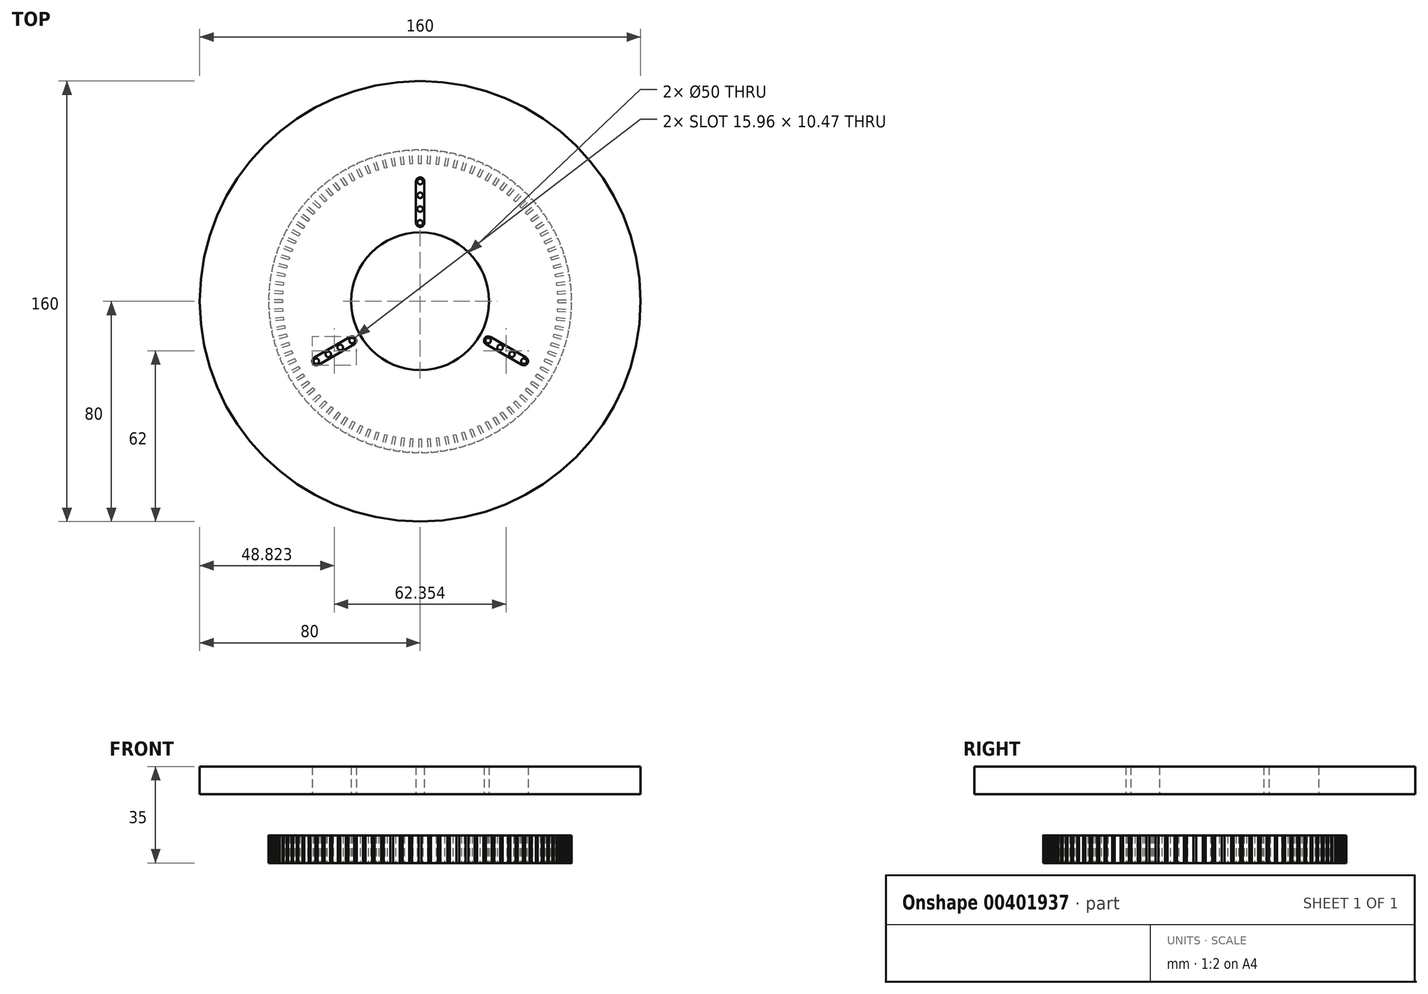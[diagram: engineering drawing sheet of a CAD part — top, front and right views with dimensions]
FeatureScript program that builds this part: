
annotation { "Feature Type Name" : "Feature", "Feature Type Description" : "" }
export const myFeature = defineFeature(function(context is Context, id is Id, definition is map)
    precondition{}
    {
        {
            var Q0;
            Q0=qCreatedBy(makeId("Top.planeOp"),FACE);
            var sketch = newSketch(context, id + "F0", { "sketchPlane" : qUnion([Q0])});
            skCircle(sketch, "E0", {"center": v(0, 0) * mm, "radius": 55 * mm});
            skCircle(sketch, "E1", {"center": v(0, 0) * mm, "radius": 25 * mm});
            skLineSegment(sketch, "E2.bottom", {"start": v(0.5, 50) * mm, "end": v(-0.5, 50) * mm});
            skLineSegment(sketch, "E2.top", {"start": v(0.5, 60) * mm, "end": v(-0.5, 60) * mm});
            skLineSegment(sketch, "E2.left", {"start": v(0.5, 50) * mm, "end": v(0.5, 60) * mm});
            skLineSegment(sketch, "E2.right", {"start": v(-0.5, 50) * mm, "end": v(-0.5, 60) * mm});
            skPoint(sketch, "E2.middle", {"position": v(0, 55) * mm});
            skLineSegment(sketch, "E3.1.0", {"start": v(-2.64, 49.93) * mm, "end": v(-3.27, 59.91) * mm});
            skLineSegment(sketch, "E3.1.1", {"start": v(-2.64, 49.93) * mm, "end": v(-3.64, 49.87) * mm});
            skLineSegment(sketch, "E3.1.2", {"start": v(-3.64, 49.87) * mm, "end": v(-4.27, 59.85) * mm});
            skLineSegment(sketch, "E3.1.3", {"start": v(-3.27, 59.91) * mm, "end": v(-4.27, 59.85) * mm});
            skLineSegment(sketch, "E3.2.0", {"start": v(-5.77, 49.67) * mm, "end": v(-7.02, 59.59) * mm});
            skLineSegment(sketch, "E3.2.1", {"start": v(-5.77, 49.67) * mm, "end": v(-6.76, 49.54) * mm});
            skLineSegment(sketch, "E3.2.2", {"start": v(-6.76, 49.54) * mm, "end": v(-8.02, 59.46) * mm});
            skLineSegment(sketch, "E3.2.3", {"start": v(-7.02, 59.59) * mm, "end": v(-8.02, 59.46) * mm});
            skLineSegment(sketch, "E4.1.3.0", {"start": v(-8.88, 49.2) * mm, "end": v(-10.75, 59.03) * mm});
            skLineSegment(sketch, "E4.3.3.0", {"start": v(-8.88, 49.2) * mm, "end": v(-9.86, 49.02) * mm});
            skLineSegment(sketch, "E4.6.3.0", {"start": v(-9.86, 49.02) * mm, "end": v(-11.73, 58.84) * mm});
            skLineSegment(sketch, "E4.9.3.0", {"start": v(-10.75, 59.03) * mm, "end": v(-11.73, 58.84) * mm});
            skLineSegment(sketch, "E4.1.4.0", {"start": v(-11.95, 48.55) * mm, "end": v(-14.44, 58.24) * mm});
            skLineSegment(sketch, "E4.3.4.0", {"start": v(-11.95, 48.55) * mm, "end": v(-12.92, 48.3) * mm});
            skLineSegment(sketch, "E4.6.4.0", {"start": v(-12.92, 48.3) * mm, "end": v(-15.4, 58) * mm});
            skLineSegment(sketch, "E4.9.4.0", {"start": v(-14.44, 58.24) * mm, "end": v(-15.4, 58) * mm});
            skLineSegment(sketch, "E4.1.5.0", {"start": v(-14.98, 47.7) * mm, "end": v(-18.07, 57.22) * mm});
            skLineSegment(sketch, "E4.3.5.0", {"start": v(-14.98, 47.7) * mm, "end": v(-15.93, 47.4) * mm});
            skLineSegment(sketch, "E4.6.5.0", {"start": v(-15.93, 47.4) * mm, "end": v(-19.02, 56.9) * mm});
            skLineSegment(sketch, "E4.9.5.0", {"start": v(-18.07, 57.22) * mm, "end": v(-19.02, 56.9) * mm});
            skLineSegment(sketch, "E4.1.6.0", {"start": v(-17.94, 46.67) * mm, "end": v(-21.62, 55.97) * mm});
            skLineSegment(sketch, "E4.3.6.0", {"start": v(-17.94, 46.67) * mm, "end": v(-18.87, 46.3) * mm});
            skLineSegment(sketch, "E4.6.6.0", {"start": v(-18.87, 46.3) * mm, "end": v(-22.55, 55.6) * mm});
            skLineSegment(sketch, "E4.9.6.0", {"start": v(-21.62, 55.97) * mm, "end": v(-22.55, 55.6) * mm});
            skLineSegment(sketch, "E4.1.7.0", {"start": v(-20.84, 45.45) * mm, "end": v(-25.1, 54.5) * mm});
            skLineSegment(sketch, "E4.3.7.0", {"start": v(-20.84, 45.45) * mm, "end": v(-21.74, 45.03) * mm});
            skLineSegment(sketch, "E4.6.7.0", {"start": v(-21.74, 45.03) * mm, "end": v(-26, 54.08) * mm});
            skLineSegment(sketch, "E4.9.7.0", {"start": v(-25.1, 54.5) * mm, "end": v(-26, 54.08) * mm});
            skLineSegment(sketch, "E4.1.8.0", {"start": v(-23.65, 44.06) * mm, "end": v(-28.47, 52.82) * mm});
            skLineSegment(sketch, "E4.3.8.0", {"start": v(-23.65, 44.06) * mm, "end": v(-24.53, 43.57) * mm});
            skLineSegment(sketch, "E4.6.8.0", {"start": v(-24.53, 43.57) * mm, "end": v(-29.34, 52.34) * mm});
            skLineSegment(sketch, "E4.9.8.0", {"start": v(-28.47, 52.82) * mm, "end": v(-29.34, 52.34) * mm});
            skLineSegment(sketch, "E4.1.9.0", {"start": v(-26.37, 42.48) * mm, "end": v(-31.73, 50.93) * mm});
            skLineSegment(sketch, "E4.3.9.0", {"start": v(-26.37, 42.48) * mm, "end": v(-27.21, 41.95) * mm});
            skLineSegment(sketch, "E4.6.9.0", {"start": v(-27.21, 41.95) * mm, "end": v(-32.57, 50.4) * mm});
            skLineSegment(sketch, "E4.9.9.0", {"start": v(-31.73, 50.93) * mm, "end": v(-32.57, 50.4) * mm});
            skLineSegment(sketch, "E4.1.10.0", {"start": v(-28.98, 40.74) * mm, "end": v(-34.86, 48.83) * mm});
            skLineSegment(sketch, "E4.3.10.0", {"start": v(-28.98, 40.74) * mm, "end": v(-29.8, 40.16) * mm});
            skLineSegment(sketch, "E4.6.10.0", {"start": v(-29.8, 40.16) * mm, "end": v(-35.67, 48.25) * mm});
            skLineSegment(sketch, "E4.9.10.0", {"start": v(-34.86, 48.83) * mm, "end": v(-35.67, 48.25) * mm});
            skLineSegment(sketch, "E4.1.11.0", {"start": v(-31.49, 38.84) * mm, "end": v(-37.86, 46.55) * mm});
            skLineSegment(sketch, "E4.3.11.0", {"start": v(-31.49, 38.84) * mm, "end": v(-32.26, 38.2) * mm});
            skLineSegment(sketch, "E4.6.11.0", {"start": v(-32.26, 38.2) * mm, "end": v(-38.63, 45.91) * mm});
            skLineSegment(sketch, "E4.9.11.0", {"start": v(-37.86, 46.55) * mm, "end": v(-38.63, 45.91) * mm});
            skLineSegment(sketch, "E4.1.12.0", {"start": v(-33.86, 36.8) * mm, "end": v(-40.7, 44.08) * mm});
            skLineSegment(sketch, "E4.3.12.0", {"start": v(-33.86, 36.8) * mm, "end": v(-34.6, 36.1) * mm});
            skLineSegment(sketch, "E4.6.12.0", {"start": v(-34.6, 36.1) * mm, "end": v(-41.44, 43.4) * mm});
            skLineSegment(sketch, "E4.9.12.0", {"start": v(-40.7, 44.08) * mm, "end": v(-41.44, 43.4) * mm});
            skLineSegment(sketch, "E4.1.13.0", {"start": v(-36.1, 34.6) * mm, "end": v(-43.4, 41.44) * mm});
            skLineSegment(sketch, "E4.3.13.0", {"start": v(-36.1, 34.6) * mm, "end": v(-36.8, 33.86) * mm});
            skLineSegment(sketch, "E4.6.13.0", {"start": v(-36.8, 33.86) * mm, "end": v(-44.08, 40.7) * mm});
            skLineSegment(sketch, "E4.9.13.0", {"start": v(-43.4, 41.44) * mm, "end": v(-44.08, 40.7) * mm});
            skLineSegment(sketch, "E4.1.14.0", {"start": v(-38.2, 32.26) * mm, "end": v(-45.91, 38.63) * mm});
            skLineSegment(sketch, "E4.3.14.0", {"start": v(-38.2, 32.26) * mm, "end": v(-38.84, 31.49) * mm});
            skLineSegment(sketch, "E4.6.14.0", {"start": v(-38.84, 31.49) * mm, "end": v(-46.55, 37.86) * mm});
            skLineSegment(sketch, "E4.9.14.0", {"start": v(-45.91, 38.63) * mm, "end": v(-46.55, 37.86) * mm});
            skLineSegment(sketch, "E4.1.15.0", {"start": v(-40.16, 29.8) * mm, "end": v(-48.25, 35.67) * mm});
            skLineSegment(sketch, "E4.3.15.0", {"start": v(-40.16, 29.8) * mm, "end": v(-40.74, 28.98) * mm});
            skLineSegment(sketch, "E4.6.15.0", {"start": v(-40.74, 28.98) * mm, "end": v(-48.83, 34.86) * mm});
            skLineSegment(sketch, "E4.9.15.0", {"start": v(-48.25, 35.67) * mm, "end": v(-48.83, 34.86) * mm});
            skLineSegment(sketch, "E4.1.16.0", {"start": v(-41.95, 27.21) * mm, "end": v(-50.4, 32.57) * mm});
            skLineSegment(sketch, "E4.3.16.0", {"start": v(-41.95, 27.21) * mm, "end": v(-42.48, 26.37) * mm});
            skLineSegment(sketch, "E4.6.16.0", {"start": v(-42.48, 26.37) * mm, "end": v(-50.93, 31.73) * mm});
            skLineSegment(sketch, "E4.9.16.0", {"start": v(-50.4, 32.57) * mm, "end": v(-50.93, 31.73) * mm});
            skLineSegment(sketch, "E4.1.17.0", {"start": v(-43.57, 24.53) * mm, "end": v(-52.34, 29.34) * mm});
            skLineSegment(sketch, "E4.3.17.0", {"start": v(-43.57, 24.53) * mm, "end": v(-44.06, 23.65) * mm});
            skLineSegment(sketch, "E4.6.17.0", {"start": v(-44.06, 23.65) * mm, "end": v(-52.82, 28.47) * mm});
            skLineSegment(sketch, "E4.9.17.0", {"start": v(-52.34, 29.34) * mm, "end": v(-52.82, 28.47) * mm});
            skLineSegment(sketch, "E4.1.18.0", {"start": v(-45.03, 21.74) * mm, "end": v(-54.08, 26) * mm});
            skLineSegment(sketch, "E4.3.18.0", {"start": v(-45.03, 21.74) * mm, "end": v(-45.45, 20.84) * mm});
            skLineSegment(sketch, "E4.6.18.0", {"start": v(-45.45, 20.84) * mm, "end": v(-54.5, 25.1) * mm});
            skLineSegment(sketch, "E4.9.18.0", {"start": v(-54.08, 26) * mm, "end": v(-54.5, 25.1) * mm});
            skLineSegment(sketch, "E4.1.19.0", {"start": v(-46.3, 18.87) * mm, "end": v(-55.6, 22.55) * mm});
            skLineSegment(sketch, "E4.3.19.0", {"start": v(-46.3, 18.87) * mm, "end": v(-46.67, 17.94) * mm});
            skLineSegment(sketch, "E4.6.19.0", {"start": v(-46.67, 17.94) * mm, "end": v(-55.97, 21.62) * mm});
            skLineSegment(sketch, "E4.9.19.0", {"start": v(-55.6, 22.55) * mm, "end": v(-55.97, 21.62) * mm});
            skLineSegment(sketch, "E4.1.20.0", {"start": v(-47.4, 15.93) * mm, "end": v(-56.9, 19.02) * mm});
            skLineSegment(sketch, "E4.3.20.0", {"start": v(-47.4, 15.93) * mm, "end": v(-47.7, 14.98) * mm});
            skLineSegment(sketch, "E4.6.20.0", {"start": v(-47.7, 14.98) * mm, "end": v(-57.22, 18.07) * mm});
            skLineSegment(sketch, "E4.9.20.0", {"start": v(-56.9, 19.02) * mm, "end": v(-57.22, 18.07) * mm});
            skLineSegment(sketch, "E4.1.21.0", {"start": v(-48.3, 12.92) * mm, "end": v(-58, 15.4) * mm});
            skLineSegment(sketch, "E4.3.21.0", {"start": v(-48.3, 12.92) * mm, "end": v(-48.55, 11.95) * mm});
            skLineSegment(sketch, "E4.6.21.0", {"start": v(-48.55, 11.95) * mm, "end": v(-58.24, 14.44) * mm});
            skLineSegment(sketch, "E4.9.21.0", {"start": v(-58, 15.4) * mm, "end": v(-58.24, 14.44) * mm});
            skLineSegment(sketch, "E4.1.22.0", {"start": v(-49.02, 9.86) * mm, "end": v(-58.84, 11.73) * mm});
            skLineSegment(sketch, "E4.3.22.0", {"start": v(-49.02, 9.86) * mm, "end": v(-49.2, 8.88) * mm});
            skLineSegment(sketch, "E4.6.22.0", {"start": v(-49.2, 8.88) * mm, "end": v(-59.03, 10.75) * mm});
            skLineSegment(sketch, "E4.9.22.0", {"start": v(-58.84, 11.73) * mm, "end": v(-59.03, 10.75) * mm});
            skLineSegment(sketch, "E4.1.23.0", {"start": v(-49.54, 6.76) * mm, "end": v(-59.46, 8.02) * mm});
            skLineSegment(sketch, "E4.3.23.0", {"start": v(-49.54, 6.76) * mm, "end": v(-49.67, 5.77) * mm});
            skLineSegment(sketch, "E4.6.23.0", {"start": v(-49.67, 5.77) * mm, "end": v(-59.59, 7.02) * mm});
            skLineSegment(sketch, "E4.9.23.0", {"start": v(-59.46, 8.02) * mm, "end": v(-59.59, 7.02) * mm});
            skLineSegment(sketch, "E4.1.24.0", {"start": v(-49.87, 3.64) * mm, "end": v(-59.85, 4.27) * mm});
            skLineSegment(sketch, "E4.3.24.0", {"start": v(-49.87, 3.64) * mm, "end": v(-49.93, 2.64) * mm});
            skLineSegment(sketch, "E4.6.24.0", {"start": v(-49.93, 2.64) * mm, "end": v(-59.91, 3.27) * mm});
            skLineSegment(sketch, "E4.9.24.0", {"start": v(-59.85, 4.27) * mm, "end": v(-59.91, 3.27) * mm});
            skLineSegment(sketch, "E4.1.25.0", {"start": v(-50, 0.5) * mm, "end": v(-60, 0.5) * mm});
            skLineSegment(sketch, "E4.3.25.0", {"start": v(-50, 0.5) * mm, "end": v(-50, -0.5) * mm});
            skLineSegment(sketch, "E4.6.25.0", {"start": v(-50, -0.5) * mm, "end": v(-60, -0.5) * mm});
            skLineSegment(sketch, "E4.9.25.0", {"start": v(-60, 0.5) * mm, "end": v(-60, -0.5) * mm});
            skLineSegment(sketch, "E4.1.26.0", {"start": v(-49.93, -2.64) * mm, "end": v(-59.91, -3.27) * mm});
            skLineSegment(sketch, "E4.3.26.0", {"start": v(-49.93, -2.64) * mm, "end": v(-49.87, -3.64) * mm});
            skLineSegment(sketch, "E4.6.26.0", {"start": v(-49.87, -3.64) * mm, "end": v(-59.85, -4.27) * mm});
            skLineSegment(sketch, "E4.9.26.0", {"start": v(-59.91, -3.27) * mm, "end": v(-59.85, -4.27) * mm});
            skLineSegment(sketch, "E4.1.27.0", {"start": v(-49.67, -5.77) * mm, "end": v(-59.59, -7.02) * mm});
            skLineSegment(sketch, "E4.3.27.0", {"start": v(-49.67, -5.77) * mm, "end": v(-49.54, -6.76) * mm});
            skLineSegment(sketch, "E4.6.27.0", {"start": v(-49.54, -6.76) * mm, "end": v(-59.46, -8.02) * mm});
            skLineSegment(sketch, "E4.9.27.0", {"start": v(-59.59, -7.02) * mm, "end": v(-59.46, -8.02) * mm});
            skLineSegment(sketch, "E4.1.28.0", {"start": v(-49.2, -8.88) * mm, "end": v(-59.03, -10.75) * mm});
            skLineSegment(sketch, "E4.3.28.0", {"start": v(-49.2, -8.88) * mm, "end": v(-49.02, -9.86) * mm});
            skLineSegment(sketch, "E4.6.28.0", {"start": v(-49.02, -9.86) * mm, "end": v(-58.84, -11.73) * mm});
            skLineSegment(sketch, "E4.9.28.0", {"start": v(-59.03, -10.75) * mm, "end": v(-58.84, -11.73) * mm});
            skLineSegment(sketch, "E4.1.29.0", {"start": v(-48.55, -11.95) * mm, "end": v(-58.24, -14.44) * mm});
            skLineSegment(sketch, "E4.3.29.0", {"start": v(-48.55, -11.95) * mm, "end": v(-48.3, -12.92) * mm});
            skLineSegment(sketch, "E4.6.29.0", {"start": v(-48.3, -12.92) * mm, "end": v(-58, -15.4) * mm});
            skLineSegment(sketch, "E4.9.29.0", {"start": v(-58.24, -14.44) * mm, "end": v(-58, -15.4) * mm});
            skLineSegment(sketch, "E4.1.30.0", {"start": v(-47.7, -14.98) * mm, "end": v(-57.22, -18.07) * mm});
            skLineSegment(sketch, "E4.3.30.0", {"start": v(-47.7, -14.98) * mm, "end": v(-47.4, -15.93) * mm});
            skLineSegment(sketch, "E4.6.30.0", {"start": v(-47.4, -15.93) * mm, "end": v(-56.9, -19.02) * mm});
            skLineSegment(sketch, "E4.9.30.0", {"start": v(-57.22, -18.07) * mm, "end": v(-56.9, -19.02) * mm});
            skLineSegment(sketch, "E4.1.31.0", {"start": v(-46.67, -17.94) * mm, "end": v(-55.97, -21.62) * mm});
            skLineSegment(sketch, "E4.3.31.0", {"start": v(-46.67, -17.94) * mm, "end": v(-46.3, -18.87) * mm});
            skLineSegment(sketch, "E4.6.31.0", {"start": v(-46.3, -18.87) * mm, "end": v(-55.6, -22.55) * mm});
            skLineSegment(sketch, "E4.9.31.0", {"start": v(-55.97, -21.62) * mm, "end": v(-55.6, -22.55) * mm});
            skLineSegment(sketch, "E4.1.32.0", {"start": v(-45.45, -20.84) * mm, "end": v(-54.5, -25.1) * mm});
            skLineSegment(sketch, "E4.3.32.0", {"start": v(-45.45, -20.84) * mm, "end": v(-45.03, -21.74) * mm});
            skLineSegment(sketch, "E4.6.32.0", {"start": v(-45.03, -21.74) * mm, "end": v(-54.08, -26) * mm});
            skLineSegment(sketch, "E4.9.32.0", {"start": v(-54.5, -25.1) * mm, "end": v(-54.08, -26) * mm});
            skLineSegment(sketch, "E4.1.33.0", {"start": v(-44.06, -23.65) * mm, "end": v(-52.82, -28.47) * mm});
            skLineSegment(sketch, "E4.3.33.0", {"start": v(-44.06, -23.65) * mm, "end": v(-43.57, -24.53) * mm});
            skLineSegment(sketch, "E4.6.33.0", {"start": v(-43.57, -24.53) * mm, "end": v(-52.34, -29.34) * mm});
            skLineSegment(sketch, "E4.9.33.0", {"start": v(-52.82, -28.47) * mm, "end": v(-52.34, -29.34) * mm});
            skLineSegment(sketch, "E4.1.34.0", {"start": v(-42.48, -26.37) * mm, "end": v(-50.93, -31.73) * mm});
            skLineSegment(sketch, "E4.3.34.0", {"start": v(-42.48, -26.37) * mm, "end": v(-41.95, -27.21) * mm});
            skLineSegment(sketch, "E4.6.34.0", {"start": v(-41.95, -27.21) * mm, "end": v(-50.4, -32.57) * mm});
            skLineSegment(sketch, "E4.9.34.0", {"start": v(-50.93, -31.73) * mm, "end": v(-50.4, -32.57) * mm});
            skLineSegment(sketch, "E4.1.35.0", {"start": v(-40.74, -28.98) * mm, "end": v(-48.83, -34.86) * mm});
            skLineSegment(sketch, "E4.3.35.0", {"start": v(-40.74, -28.98) * mm, "end": v(-40.16, -29.8) * mm});
            skLineSegment(sketch, "E4.6.35.0", {"start": v(-40.16, -29.8) * mm, "end": v(-48.25, -35.67) * mm});
            skLineSegment(sketch, "E4.9.35.0", {"start": v(-48.83, -34.86) * mm, "end": v(-48.25, -35.67) * mm});
            skLineSegment(sketch, "E4.1.36.0", {"start": v(-38.84, -31.49) * mm, "end": v(-46.55, -37.86) * mm});
            skLineSegment(sketch, "E4.3.36.0", {"start": v(-38.84, -31.49) * mm, "end": v(-38.2, -32.26) * mm});
            skLineSegment(sketch, "E4.6.36.0", {"start": v(-38.2, -32.26) * mm, "end": v(-45.91, -38.63) * mm});
            skLineSegment(sketch, "E4.9.36.0", {"start": v(-46.55, -37.86) * mm, "end": v(-45.91, -38.63) * mm});
            skLineSegment(sketch, "E4.1.37.0", {"start": v(-36.8, -33.86) * mm, "end": v(-44.08, -40.7) * mm});
            skLineSegment(sketch, "E4.3.37.0", {"start": v(-36.8, -33.86) * mm, "end": v(-36.1, -34.6) * mm});
            skLineSegment(sketch, "E4.6.37.0", {"start": v(-36.1, -34.6) * mm, "end": v(-43.4, -41.44) * mm});
            skLineSegment(sketch, "E4.9.37.0", {"start": v(-44.08, -40.7) * mm, "end": v(-43.4, -41.44) * mm});
            skLineSegment(sketch, "E4.1.38.0", {"start": v(-34.6, -36.1) * mm, "end": v(-41.44, -43.4) * mm});
            skLineSegment(sketch, "E4.3.38.0", {"start": v(-34.6, -36.1) * mm, "end": v(-33.86, -36.8) * mm});
            skLineSegment(sketch, "E4.6.38.0", {"start": v(-33.86, -36.8) * mm, "end": v(-40.7, -44.08) * mm});
            skLineSegment(sketch, "E4.9.38.0", {"start": v(-41.44, -43.4) * mm, "end": v(-40.7, -44.08) * mm});
            skLineSegment(sketch, "E4.1.39.0", {"start": v(-32.26, -38.2) * mm, "end": v(-38.63, -45.91) * mm});
            skLineSegment(sketch, "E4.3.39.0", {"start": v(-32.26, -38.2) * mm, "end": v(-31.49, -38.84) * mm});
            skLineSegment(sketch, "E4.6.39.0", {"start": v(-31.49, -38.84) * mm, "end": v(-37.86, -46.55) * mm});
            skLineSegment(sketch, "E4.9.39.0", {"start": v(-38.63, -45.91) * mm, "end": v(-37.86, -46.55) * mm});
            skLineSegment(sketch, "E4.1.40.0", {"start": v(-29.8, -40.16) * mm, "end": v(-35.67, -48.25) * mm});
            skLineSegment(sketch, "E4.3.40.0", {"start": v(-29.8, -40.16) * mm, "end": v(-28.98, -40.74) * mm});
            skLineSegment(sketch, "E4.6.40.0", {"start": v(-28.98, -40.74) * mm, "end": v(-34.86, -48.83) * mm});
            skLineSegment(sketch, "E4.9.40.0", {"start": v(-35.67, -48.25) * mm, "end": v(-34.86, -48.83) * mm});
            skLineSegment(sketch, "E4.1.41.0", {"start": v(-27.21, -41.95) * mm, "end": v(-32.57, -50.4) * mm});
            skLineSegment(sketch, "E4.3.41.0", {"start": v(-27.21, -41.95) * mm, "end": v(-26.37, -42.48) * mm});
            skLineSegment(sketch, "E4.6.41.0", {"start": v(-26.37, -42.48) * mm, "end": v(-31.73, -50.93) * mm});
            skLineSegment(sketch, "E4.9.41.0", {"start": v(-32.57, -50.4) * mm, "end": v(-31.73, -50.93) * mm});
            skLineSegment(sketch, "E4.1.42.0", {"start": v(-24.53, -43.57) * mm, "end": v(-29.34, -52.34) * mm});
            skLineSegment(sketch, "E4.3.42.0", {"start": v(-24.53, -43.57) * mm, "end": v(-23.65, -44.06) * mm});
            skLineSegment(sketch, "E4.6.42.0", {"start": v(-23.65, -44.06) * mm, "end": v(-28.47, -52.82) * mm});
            skLineSegment(sketch, "E4.9.42.0", {"start": v(-29.34, -52.34) * mm, "end": v(-28.47, -52.82) * mm});
            skLineSegment(sketch, "E4.1.43.0", {"start": v(-21.74, -45.03) * mm, "end": v(-26, -54.08) * mm});
            skLineSegment(sketch, "E4.3.43.0", {"start": v(-21.74, -45.03) * mm, "end": v(-20.84, -45.45) * mm});
            skLineSegment(sketch, "E4.6.43.0", {"start": v(-20.84, -45.45) * mm, "end": v(-25.1, -54.5) * mm});
            skLineSegment(sketch, "E4.9.43.0", {"start": v(-26, -54.08) * mm, "end": v(-25.1, -54.5) * mm});
            skLineSegment(sketch, "E4.1.44.0", {"start": v(-18.87, -46.3) * mm, "end": v(-22.55, -55.6) * mm});
            skLineSegment(sketch, "E4.3.44.0", {"start": v(-18.87, -46.3) * mm, "end": v(-17.94, -46.67) * mm});
            skLineSegment(sketch, "E4.6.44.0", {"start": v(-17.94, -46.67) * mm, "end": v(-21.62, -55.97) * mm});
            skLineSegment(sketch, "E4.9.44.0", {"start": v(-22.55, -55.6) * mm, "end": v(-21.62, -55.97) * mm});
            skLineSegment(sketch, "E4.1.45.0", {"start": v(-15.93, -47.4) * mm, "end": v(-19.02, -56.9) * mm});
            skLineSegment(sketch, "E4.3.45.0", {"start": v(-15.93, -47.4) * mm, "end": v(-14.98, -47.7) * mm});
            skLineSegment(sketch, "E4.6.45.0", {"start": v(-14.98, -47.7) * mm, "end": v(-18.07, -57.22) * mm});
            skLineSegment(sketch, "E4.9.45.0", {"start": v(-19.02, -56.9) * mm, "end": v(-18.07, -57.22) * mm});
            skLineSegment(sketch, "E4.1.46.0", {"start": v(-12.92, -48.3) * mm, "end": v(-15.4, -58) * mm});
            skLineSegment(sketch, "E4.3.46.0", {"start": v(-12.92, -48.3) * mm, "end": v(-11.95, -48.55) * mm});
            skLineSegment(sketch, "E4.6.46.0", {"start": v(-11.95, -48.55) * mm, "end": v(-14.44, -58.24) * mm});
            skLineSegment(sketch, "E4.9.46.0", {"start": v(-15.4, -58) * mm, "end": v(-14.44, -58.24) * mm});
            skLineSegment(sketch, "E4.1.47.0", {"start": v(-9.86, -49.02) * mm, "end": v(-11.73, -58.84) * mm});
            skLineSegment(sketch, "E4.3.47.0", {"start": v(-9.86, -49.02) * mm, "end": v(-8.88, -49.2) * mm});
            skLineSegment(sketch, "E4.6.47.0", {"start": v(-8.88, -49.2) * mm, "end": v(-10.75, -59.03) * mm});
            skLineSegment(sketch, "E4.9.47.0", {"start": v(-11.73, -58.84) * mm, "end": v(-10.75, -59.03) * mm});
            skLineSegment(sketch, "E4.1.48.0", {"start": v(-6.76, -49.54) * mm, "end": v(-8.02, -59.46) * mm});
            skLineSegment(sketch, "E4.3.48.0", {"start": v(-6.76, -49.54) * mm, "end": v(-5.77, -49.67) * mm});
            skLineSegment(sketch, "E4.6.48.0", {"start": v(-5.77, -49.67) * mm, "end": v(-7.02, -59.59) * mm});
            skLineSegment(sketch, "E4.9.48.0", {"start": v(-8.02, -59.46) * mm, "end": v(-7.02, -59.59) * mm});
            skLineSegment(sketch, "E4.1.49.0", {"start": v(-3.64, -49.87) * mm, "end": v(-4.27, -59.85) * mm});
            skLineSegment(sketch, "E4.3.49.0", {"start": v(-3.64, -49.87) * mm, "end": v(-2.64, -49.93) * mm});
            skLineSegment(sketch, "E4.6.49.0", {"start": v(-2.64, -49.93) * mm, "end": v(-3.27, -59.91) * mm});
            skLineSegment(sketch, "E4.9.49.0", {"start": v(-4.27, -59.85) * mm, "end": v(-3.27, -59.91) * mm});
            skLineSegment(sketch, "E4.1.50.0", {"start": v(-0.5, -50) * mm, "end": v(-0.5, -60) * mm});
            skLineSegment(sketch, "E4.3.50.0", {"start": v(-0.5, -50) * mm, "end": v(0.5, -50) * mm});
            skLineSegment(sketch, "E4.6.50.0", {"start": v(0.5, -50) * mm, "end": v(0.5, -60) * mm});
            skLineSegment(sketch, "E4.9.50.0", {"start": v(-0.5, -60) * mm, "end": v(0.5, -60) * mm});
            skLineSegment(sketch, "E4.1.51.0", {"start": v(2.64, -49.93) * mm, "end": v(3.27, -59.91) * mm});
            skLineSegment(sketch, "E4.3.51.0", {"start": v(2.64, -49.93) * mm, "end": v(3.64, -49.87) * mm});
            skLineSegment(sketch, "E4.6.51.0", {"start": v(3.64, -49.87) * mm, "end": v(4.27, -59.85) * mm});
            skLineSegment(sketch, "E4.9.51.0", {"start": v(3.27, -59.91) * mm, "end": v(4.27, -59.85) * mm});
            skLineSegment(sketch, "E4.1.52.0", {"start": v(5.77, -49.67) * mm, "end": v(7.02, -59.59) * mm});
            skLineSegment(sketch, "E4.3.52.0", {"start": v(5.77, -49.67) * mm, "end": v(6.76, -49.54) * mm});
            skLineSegment(sketch, "E4.6.52.0", {"start": v(6.76, -49.54) * mm, "end": v(8.02, -59.46) * mm});
            skLineSegment(sketch, "E4.9.52.0", {"start": v(7.02, -59.59) * mm, "end": v(8.02, -59.46) * mm});
            skLineSegment(sketch, "E4.1.53.0", {"start": v(8.88, -49.2) * mm, "end": v(10.75, -59.03) * mm});
            skLineSegment(sketch, "E4.3.53.0", {"start": v(8.88, -49.2) * mm, "end": v(9.86, -49.02) * mm});
            skLineSegment(sketch, "E4.6.53.0", {"start": v(9.86, -49.02) * mm, "end": v(11.73, -58.84) * mm});
            skLineSegment(sketch, "E4.9.53.0", {"start": v(10.75, -59.03) * mm, "end": v(11.73, -58.84) * mm});
            skLineSegment(sketch, "E4.1.54.0", {"start": v(11.95, -48.55) * mm, "end": v(14.44, -58.24) * mm});
            skLineSegment(sketch, "E4.3.54.0", {"start": v(11.95, -48.55) * mm, "end": v(12.92, -48.3) * mm});
            skLineSegment(sketch, "E4.6.54.0", {"start": v(12.92, -48.3) * mm, "end": v(15.4, -58) * mm});
            skLineSegment(sketch, "E4.9.54.0", {"start": v(14.44, -58.24) * mm, "end": v(15.4, -58) * mm});
            skLineSegment(sketch, "E4.1.55.0", {"start": v(14.98, -47.7) * mm, "end": v(18.07, -57.22) * mm});
            skLineSegment(sketch, "E4.3.55.0", {"start": v(14.98, -47.7) * mm, "end": v(15.93, -47.4) * mm});
            skLineSegment(sketch, "E4.6.55.0", {"start": v(15.93, -47.4) * mm, "end": v(19.02, -56.9) * mm});
            skLineSegment(sketch, "E4.9.55.0", {"start": v(18.07, -57.22) * mm, "end": v(19.02, -56.9) * mm});
            skLineSegment(sketch, "E4.1.56.0", {"start": v(17.94, -46.67) * mm, "end": v(21.62, -55.97) * mm});
            skLineSegment(sketch, "E4.3.56.0", {"start": v(17.94, -46.67) * mm, "end": v(18.87, -46.3) * mm});
            skLineSegment(sketch, "E4.6.56.0", {"start": v(18.87, -46.3) * mm, "end": v(22.55, -55.6) * mm});
            skLineSegment(sketch, "E4.9.56.0", {"start": v(21.62, -55.97) * mm, "end": v(22.55, -55.6) * mm});
            skLineSegment(sketch, "E4.1.57.0", {"start": v(20.84, -45.45) * mm, "end": v(25.1, -54.5) * mm});
            skLineSegment(sketch, "E4.3.57.0", {"start": v(20.84, -45.45) * mm, "end": v(21.74, -45.03) * mm});
            skLineSegment(sketch, "E4.6.57.0", {"start": v(21.74, -45.03) * mm, "end": v(26, -54.08) * mm});
            skLineSegment(sketch, "E4.9.57.0", {"start": v(25.1, -54.5) * mm, "end": v(26, -54.08) * mm});
            skLineSegment(sketch, "E4.1.58.0", {"start": v(23.65, -44.06) * mm, "end": v(28.47, -52.82) * mm});
            skLineSegment(sketch, "E4.3.58.0", {"start": v(23.65, -44.06) * mm, "end": v(24.53, -43.57) * mm});
            skLineSegment(sketch, "E4.6.58.0", {"start": v(24.53, -43.57) * mm, "end": v(29.34, -52.34) * mm});
            skLineSegment(sketch, "E4.9.58.0", {"start": v(28.47, -52.82) * mm, "end": v(29.34, -52.34) * mm});
            skLineSegment(sketch, "E4.1.59.0", {"start": v(26.37, -42.48) * mm, "end": v(31.73, -50.93) * mm});
            skLineSegment(sketch, "E4.3.59.0", {"start": v(26.37, -42.48) * mm, "end": v(27.21, -41.95) * mm});
            skLineSegment(sketch, "E4.6.59.0", {"start": v(27.21, -41.95) * mm, "end": v(32.57, -50.4) * mm});
            skLineSegment(sketch, "E4.9.59.0", {"start": v(31.73, -50.93) * mm, "end": v(32.57, -50.4) * mm});
            skLineSegment(sketch, "E4.1.60.0", {"start": v(28.98, -40.74) * mm, "end": v(34.86, -48.83) * mm});
            skLineSegment(sketch, "E4.3.60.0", {"start": v(28.98, -40.74) * mm, "end": v(29.8, -40.16) * mm});
            skLineSegment(sketch, "E4.6.60.0", {"start": v(29.8, -40.16) * mm, "end": v(35.67, -48.25) * mm});
            skLineSegment(sketch, "E4.9.60.0", {"start": v(34.86, -48.83) * mm, "end": v(35.67, -48.25) * mm});
            skLineSegment(sketch, "E4.1.61.0", {"start": v(31.49, -38.84) * mm, "end": v(37.86, -46.55) * mm});
            skLineSegment(sketch, "E4.3.61.0", {"start": v(31.49, -38.84) * mm, "end": v(32.26, -38.2) * mm});
            skLineSegment(sketch, "E4.6.61.0", {"start": v(32.26, -38.2) * mm, "end": v(38.63, -45.91) * mm});
            skLineSegment(sketch, "E4.9.61.0", {"start": v(37.86, -46.55) * mm, "end": v(38.63, -45.91) * mm});
            skLineSegment(sketch, "E4.1.62.0", {"start": v(33.86, -36.8) * mm, "end": v(40.7, -44.08) * mm});
            skLineSegment(sketch, "E4.3.62.0", {"start": v(33.86, -36.8) * mm, "end": v(34.6, -36.1) * mm});
            skLineSegment(sketch, "E4.6.62.0", {"start": v(34.6, -36.1) * mm, "end": v(41.44, -43.4) * mm});
            skLineSegment(sketch, "E4.9.62.0", {"start": v(40.7, -44.08) * mm, "end": v(41.44, -43.4) * mm});
            skLineSegment(sketch, "E4.1.63.0", {"start": v(36.1, -34.6) * mm, "end": v(43.4, -41.44) * mm});
            skLineSegment(sketch, "E4.3.63.0", {"start": v(36.1, -34.6) * mm, "end": v(36.8, -33.86) * mm});
            skLineSegment(sketch, "E4.6.63.0", {"start": v(36.8, -33.86) * mm, "end": v(44.08, -40.7) * mm});
            skLineSegment(sketch, "E4.9.63.0", {"start": v(43.4, -41.44) * mm, "end": v(44.08, -40.7) * mm});
            skLineSegment(sketch, "E4.1.64.0", {"start": v(38.2, -32.26) * mm, "end": v(45.91, -38.63) * mm});
            skLineSegment(sketch, "E4.3.64.0", {"start": v(38.2, -32.26) * mm, "end": v(38.84, -31.49) * mm});
            skLineSegment(sketch, "E4.6.64.0", {"start": v(38.84, -31.49) * mm, "end": v(46.55, -37.86) * mm});
            skLineSegment(sketch, "E4.9.64.0", {"start": v(45.91, -38.63) * mm, "end": v(46.55, -37.86) * mm});
            skLineSegment(sketch, "E4.1.65.0", {"start": v(40.16, -29.8) * mm, "end": v(48.25, -35.67) * mm});
            skLineSegment(sketch, "E4.3.65.0", {"start": v(40.16, -29.8) * mm, "end": v(40.74, -28.98) * mm});
            skLineSegment(sketch, "E4.6.65.0", {"start": v(40.74, -28.98) * mm, "end": v(48.83, -34.86) * mm});
            skLineSegment(sketch, "E4.9.65.0", {"start": v(48.25, -35.67) * mm, "end": v(48.83, -34.86) * mm});
            skLineSegment(sketch, "E4.1.66.0", {"start": v(41.95, -27.21) * mm, "end": v(50.4, -32.57) * mm});
            skLineSegment(sketch, "E4.3.66.0", {"start": v(41.95, -27.21) * mm, "end": v(42.48, -26.37) * mm});
            skLineSegment(sketch, "E4.6.66.0", {"start": v(42.48, -26.37) * mm, "end": v(50.93, -31.73) * mm});
            skLineSegment(sketch, "E4.9.66.0", {"start": v(50.4, -32.57) * mm, "end": v(50.93, -31.73) * mm});
            skLineSegment(sketch, "E4.1.67.0", {"start": v(43.57, -24.53) * mm, "end": v(52.34, -29.34) * mm});
            skLineSegment(sketch, "E4.3.67.0", {"start": v(43.57, -24.53) * mm, "end": v(44.06, -23.65) * mm});
            skLineSegment(sketch, "E4.6.67.0", {"start": v(44.06, -23.65) * mm, "end": v(52.82, -28.47) * mm});
            skLineSegment(sketch, "E4.9.67.0", {"start": v(52.34, -29.34) * mm, "end": v(52.82, -28.47) * mm});
            skLineSegment(sketch, "E4.1.68.0", {"start": v(45.03, -21.74) * mm, "end": v(54.08, -26) * mm});
            skLineSegment(sketch, "E4.3.68.0", {"start": v(45.03, -21.74) * mm, "end": v(45.45, -20.84) * mm});
            skLineSegment(sketch, "E4.6.68.0", {"start": v(45.45, -20.84) * mm, "end": v(54.5, -25.1) * mm});
            skLineSegment(sketch, "E4.9.68.0", {"start": v(54.08, -26) * mm, "end": v(54.5, -25.1) * mm});
            skLineSegment(sketch, "E4.1.69.0", {"start": v(46.3, -18.87) * mm, "end": v(55.6, -22.55) * mm});
            skLineSegment(sketch, "E4.3.69.0", {"start": v(46.3, -18.87) * mm, "end": v(46.67, -17.94) * mm});
            skLineSegment(sketch, "E4.6.69.0", {"start": v(46.67, -17.94) * mm, "end": v(55.97, -21.62) * mm});
            skLineSegment(sketch, "E4.9.69.0", {"start": v(55.6, -22.55) * mm, "end": v(55.97, -21.62) * mm});
            skLineSegment(sketch, "E4.1.70.0", {"start": v(47.4, -15.93) * mm, "end": v(56.9, -19.02) * mm});
            skLineSegment(sketch, "E4.3.70.0", {"start": v(47.4, -15.93) * mm, "end": v(47.7, -14.98) * mm});
            skLineSegment(sketch, "E4.6.70.0", {"start": v(47.7, -14.98) * mm, "end": v(57.22, -18.07) * mm});
            skLineSegment(sketch, "E4.9.70.0", {"start": v(56.9, -19.02) * mm, "end": v(57.22, -18.07) * mm});
            skLineSegment(sketch, "E4.1.71.0", {"start": v(48.3, -12.92) * mm, "end": v(58, -15.4) * mm});
            skLineSegment(sketch, "E4.3.71.0", {"start": v(48.3, -12.92) * mm, "end": v(48.55, -11.95) * mm});
            skLineSegment(sketch, "E4.6.71.0", {"start": v(48.55, -11.95) * mm, "end": v(58.24, -14.44) * mm});
            skLineSegment(sketch, "E4.9.71.0", {"start": v(58, -15.4) * mm, "end": v(58.24, -14.44) * mm});
            skLineSegment(sketch, "E4.1.72.0", {"start": v(49.02, -9.86) * mm, "end": v(58.84, -11.73) * mm});
            skLineSegment(sketch, "E4.3.72.0", {"start": v(49.02, -9.86) * mm, "end": v(49.2, -8.88) * mm});
            skLineSegment(sketch, "E4.6.72.0", {"start": v(49.2, -8.88) * mm, "end": v(59.03, -10.75) * mm});
            skLineSegment(sketch, "E4.9.72.0", {"start": v(58.84, -11.73) * mm, "end": v(59.03, -10.75) * mm});
            skLineSegment(sketch, "E4.1.73.0", {"start": v(49.54, -6.76) * mm, "end": v(59.46, -8.02) * mm});
            skLineSegment(sketch, "E4.3.73.0", {"start": v(49.54, -6.76) * mm, "end": v(49.67, -5.77) * mm});
            skLineSegment(sketch, "E4.6.73.0", {"start": v(49.67, -5.77) * mm, "end": v(59.59, -7.02) * mm});
            skLineSegment(sketch, "E4.9.73.0", {"start": v(59.46, -8.02) * mm, "end": v(59.59, -7.02) * mm});
            skLineSegment(sketch, "E4.1.74.0", {"start": v(49.87, -3.64) * mm, "end": v(59.85, -4.27) * mm});
            skLineSegment(sketch, "E4.3.74.0", {"start": v(49.87, -3.64) * mm, "end": v(49.93, -2.64) * mm});
            skLineSegment(sketch, "E4.6.74.0", {"start": v(49.93, -2.64) * mm, "end": v(59.91, -3.27) * mm});
            skLineSegment(sketch, "E4.9.74.0", {"start": v(59.85, -4.27) * mm, "end": v(59.91, -3.27) * mm});
            skLineSegment(sketch, "E4.1.75.0", {"start": v(50, -0.5) * mm, "end": v(60, -0.5) * mm});
            skLineSegment(sketch, "E4.3.75.0", {"start": v(50, -0.5) * mm, "end": v(50, 0.5) * mm});
            skLineSegment(sketch, "E4.6.75.0", {"start": v(50, 0.5) * mm, "end": v(60, 0.5) * mm});
            skLineSegment(sketch, "E4.9.75.0", {"start": v(60, -0.5) * mm, "end": v(60, 0.5) * mm});
            skLineSegment(sketch, "E4.1.76.0", {"start": v(49.93, 2.64) * mm, "end": v(59.91, 3.27) * mm});
            skLineSegment(sketch, "E4.3.76.0", {"start": v(49.93, 2.64) * mm, "end": v(49.87, 3.64) * mm});
            skLineSegment(sketch, "E4.6.76.0", {"start": v(49.87, 3.64) * mm, "end": v(59.85, 4.27) * mm});
            skLineSegment(sketch, "E4.9.76.0", {"start": v(59.91, 3.27) * mm, "end": v(59.85, 4.27) * mm});
            skLineSegment(sketch, "E4.1.77.0", {"start": v(49.67, 5.77) * mm, "end": v(59.59, 7.02) * mm});
            skLineSegment(sketch, "E4.3.77.0", {"start": v(49.67, 5.77) * mm, "end": v(49.54, 6.76) * mm});
            skLineSegment(sketch, "E4.6.77.0", {"start": v(49.54, 6.76) * mm, "end": v(59.46, 8.02) * mm});
            skLineSegment(sketch, "E4.9.77.0", {"start": v(59.59, 7.02) * mm, "end": v(59.46, 8.02) * mm});
            skLineSegment(sketch, "E4.1.78.0", {"start": v(49.2, 8.88) * mm, "end": v(59.03, 10.75) * mm});
            skLineSegment(sketch, "E4.3.78.0", {"start": v(49.2, 8.88) * mm, "end": v(49.02, 9.86) * mm});
            skLineSegment(sketch, "E4.6.78.0", {"start": v(49.02, 9.86) * mm, "end": v(58.84, 11.73) * mm});
            skLineSegment(sketch, "E4.9.78.0", {"start": v(59.03, 10.75) * mm, "end": v(58.84, 11.73) * mm});
            skLineSegment(sketch, "E4.1.79.0", {"start": v(48.55, 11.95) * mm, "end": v(58.24, 14.44) * mm});
            skLineSegment(sketch, "E4.3.79.0", {"start": v(48.55, 11.95) * mm, "end": v(48.3, 12.92) * mm});
            skLineSegment(sketch, "E4.6.79.0", {"start": v(48.3, 12.92) * mm, "end": v(58, 15.4) * mm});
            skLineSegment(sketch, "E4.9.79.0", {"start": v(58.24, 14.44) * mm, "end": v(58, 15.4) * mm});
            skLineSegment(sketch, "E4.1.80.0", {"start": v(47.7, 14.98) * mm, "end": v(57.22, 18.07) * mm});
            skLineSegment(sketch, "E4.3.80.0", {"start": v(47.7, 14.98) * mm, "end": v(47.4, 15.93) * mm});
            skLineSegment(sketch, "E4.6.80.0", {"start": v(47.4, 15.93) * mm, "end": v(56.9, 19.02) * mm});
            skLineSegment(sketch, "E4.9.80.0", {"start": v(57.22, 18.07) * mm, "end": v(56.9, 19.02) * mm});
            skLineSegment(sketch, "E4.1.81.0", {"start": v(46.67, 17.94) * mm, "end": v(55.97, 21.62) * mm});
            skLineSegment(sketch, "E4.3.81.0", {"start": v(46.67, 17.94) * mm, "end": v(46.3, 18.87) * mm});
            skLineSegment(sketch, "E4.6.81.0", {"start": v(46.3, 18.87) * mm, "end": v(55.6, 22.55) * mm});
            skLineSegment(sketch, "E4.9.81.0", {"start": v(55.97, 21.62) * mm, "end": v(55.6, 22.55) * mm});
            skLineSegment(sketch, "E4.1.82.0", {"start": v(45.45, 20.84) * mm, "end": v(54.5, 25.1) * mm});
            skLineSegment(sketch, "E4.3.82.0", {"start": v(45.45, 20.84) * mm, "end": v(45.03, 21.74) * mm});
            skLineSegment(sketch, "E4.6.82.0", {"start": v(45.03, 21.74) * mm, "end": v(54.08, 26) * mm});
            skLineSegment(sketch, "E4.9.82.0", {"start": v(54.5, 25.1) * mm, "end": v(54.08, 26) * mm});
            skLineSegment(sketch, "E4.1.83.0", {"start": v(44.06, 23.65) * mm, "end": v(52.82, 28.47) * mm});
            skLineSegment(sketch, "E4.3.83.0", {"start": v(44.06, 23.65) * mm, "end": v(43.57, 24.53) * mm});
            skLineSegment(sketch, "E4.6.83.0", {"start": v(43.57, 24.53) * mm, "end": v(52.34, 29.34) * mm});
            skLineSegment(sketch, "E4.9.83.0", {"start": v(52.82, 28.47) * mm, "end": v(52.34, 29.34) * mm});
            skLineSegment(sketch, "E4.1.84.0", {"start": v(42.48, 26.37) * mm, "end": v(50.93, 31.73) * mm});
            skLineSegment(sketch, "E4.3.84.0", {"start": v(42.48, 26.37) * mm, "end": v(41.95, 27.21) * mm});
            skLineSegment(sketch, "E4.6.84.0", {"start": v(41.95, 27.21) * mm, "end": v(50.4, 32.57) * mm});
            skLineSegment(sketch, "E4.9.84.0", {"start": v(50.93, 31.73) * mm, "end": v(50.4, 32.57) * mm});
            skLineSegment(sketch, "E4.1.85.0", {"start": v(40.74, 28.98) * mm, "end": v(48.83, 34.86) * mm});
            skLineSegment(sketch, "E4.3.85.0", {"start": v(40.74, 28.98) * mm, "end": v(40.16, 29.8) * mm});
            skLineSegment(sketch, "E4.6.85.0", {"start": v(40.16, 29.8) * mm, "end": v(48.25, 35.67) * mm});
            skLineSegment(sketch, "E4.9.85.0", {"start": v(48.83, 34.86) * mm, "end": v(48.25, 35.67) * mm});
            skLineSegment(sketch, "E4.1.86.0", {"start": v(38.84, 31.49) * mm, "end": v(46.55, 37.86) * mm});
            skLineSegment(sketch, "E4.3.86.0", {"start": v(38.84, 31.49) * mm, "end": v(38.2, 32.26) * mm});
            skLineSegment(sketch, "E4.6.86.0", {"start": v(38.2, 32.26) * mm, "end": v(45.91, 38.63) * mm});
            skLineSegment(sketch, "E4.9.86.0", {"start": v(46.55, 37.86) * mm, "end": v(45.91, 38.63) * mm});
            skLineSegment(sketch, "E4.1.87.0", {"start": v(36.8, 33.86) * mm, "end": v(44.08, 40.7) * mm});
            skLineSegment(sketch, "E4.3.87.0", {"start": v(36.8, 33.86) * mm, "end": v(36.1, 34.6) * mm});
            skLineSegment(sketch, "E4.6.87.0", {"start": v(36.1, 34.6) * mm, "end": v(43.4, 41.44) * mm});
            skLineSegment(sketch, "E4.9.87.0", {"start": v(44.08, 40.7) * mm, "end": v(43.4, 41.44) * mm});
            skLineSegment(sketch, "E4.1.88.0", {"start": v(34.6, 36.1) * mm, "end": v(41.44, 43.4) * mm});
            skLineSegment(sketch, "E4.3.88.0", {"start": v(34.6, 36.1) * mm, "end": v(33.86, 36.8) * mm});
            skLineSegment(sketch, "E4.6.88.0", {"start": v(33.86, 36.8) * mm, "end": v(40.7, 44.08) * mm});
            skLineSegment(sketch, "E4.9.88.0", {"start": v(41.44, 43.4) * mm, "end": v(40.7, 44.08) * mm});
            skLineSegment(sketch, "E4.1.89.0", {"start": v(32.26, 38.2) * mm, "end": v(38.63, 45.91) * mm});
            skLineSegment(sketch, "E4.3.89.0", {"start": v(32.26, 38.2) * mm, "end": v(31.49, 38.84) * mm});
            skLineSegment(sketch, "E4.6.89.0", {"start": v(31.49, 38.84) * mm, "end": v(37.86, 46.55) * mm});
            skLineSegment(sketch, "E4.9.89.0", {"start": v(38.63, 45.91) * mm, "end": v(37.86, 46.55) * mm});
            skLineSegment(sketch, "E4.1.90.0", {"start": v(29.8, 40.16) * mm, "end": v(35.67, 48.25) * mm});
            skLineSegment(sketch, "E4.3.90.0", {"start": v(29.8, 40.16) * mm, "end": v(28.98, 40.74) * mm});
            skLineSegment(sketch, "E4.6.90.0", {"start": v(28.98, 40.74) * mm, "end": v(34.86, 48.83) * mm});
            skLineSegment(sketch, "E4.9.90.0", {"start": v(35.67, 48.25) * mm, "end": v(34.86, 48.83) * mm});
            skLineSegment(sketch, "E4.1.91.0", {"start": v(27.21, 41.95) * mm, "end": v(32.57, 50.4) * mm});
            skLineSegment(sketch, "E4.3.91.0", {"start": v(27.21, 41.95) * mm, "end": v(26.37, 42.48) * mm});
            skLineSegment(sketch, "E4.6.91.0", {"start": v(26.37, 42.48) * mm, "end": v(31.73, 50.93) * mm});
            skLineSegment(sketch, "E4.9.91.0", {"start": v(32.57, 50.4) * mm, "end": v(31.73, 50.93) * mm});
            skLineSegment(sketch, "E4.1.92.0", {"start": v(24.53, 43.57) * mm, "end": v(29.34, 52.34) * mm});
            skLineSegment(sketch, "E4.3.92.0", {"start": v(24.53, 43.57) * mm, "end": v(23.65, 44.06) * mm});
            skLineSegment(sketch, "E4.6.92.0", {"start": v(23.65, 44.06) * mm, "end": v(28.47, 52.82) * mm});
            skLineSegment(sketch, "E4.9.92.0", {"start": v(29.34, 52.34) * mm, "end": v(28.47, 52.82) * mm});
            skLineSegment(sketch, "E4.1.93.0", {"start": v(21.74, 45.03) * mm, "end": v(26, 54.08) * mm});
            skLineSegment(sketch, "E4.3.93.0", {"start": v(21.74, 45.03) * mm, "end": v(20.84, 45.45) * mm});
            skLineSegment(sketch, "E4.6.93.0", {"start": v(20.84, 45.45) * mm, "end": v(25.1, 54.5) * mm});
            skLineSegment(sketch, "E4.9.93.0", {"start": v(26, 54.08) * mm, "end": v(25.1, 54.5) * mm});
            skLineSegment(sketch, "E4.1.94.0", {"start": v(18.87, 46.3) * mm, "end": v(22.55, 55.6) * mm});
            skLineSegment(sketch, "E4.3.94.0", {"start": v(18.87, 46.3) * mm, "end": v(17.94, 46.67) * mm});
            skLineSegment(sketch, "E4.6.94.0", {"start": v(17.94, 46.67) * mm, "end": v(21.62, 55.97) * mm});
            skLineSegment(sketch, "E4.9.94.0", {"start": v(22.55, 55.6) * mm, "end": v(21.62, 55.97) * mm});
            skLineSegment(sketch, "E4.1.95.0", {"start": v(15.93, 47.4) * mm, "end": v(19.02, 56.9) * mm});
            skLineSegment(sketch, "E4.3.95.0", {"start": v(15.93, 47.4) * mm, "end": v(14.98, 47.7) * mm});
            skLineSegment(sketch, "E4.6.95.0", {"start": v(14.98, 47.7) * mm, "end": v(18.07, 57.22) * mm});
            skLineSegment(sketch, "E4.9.95.0", {"start": v(19.02, 56.9) * mm, "end": v(18.07, 57.22) * mm});
            skLineSegment(sketch, "E4.1.96.0", {"start": v(12.92, 48.3) * mm, "end": v(15.4, 58) * mm});
            skLineSegment(sketch, "E4.3.96.0", {"start": v(12.92, 48.3) * mm, "end": v(11.95, 48.55) * mm});
            skLineSegment(sketch, "E4.6.96.0", {"start": v(11.95, 48.55) * mm, "end": v(14.44, 58.24) * mm});
            skLineSegment(sketch, "E4.9.96.0", {"start": v(15.4, 58) * mm, "end": v(14.44, 58.24) * mm});
            skLineSegment(sketch, "E4.1.97.0", {"start": v(9.86, 49.02) * mm, "end": v(11.73, 58.84) * mm});
            skLineSegment(sketch, "E4.3.97.0", {"start": v(9.86, 49.02) * mm, "end": v(8.88, 49.2) * mm});
            skLineSegment(sketch, "E4.6.97.0", {"start": v(8.88, 49.2) * mm, "end": v(10.75, 59.03) * mm});
            skLineSegment(sketch, "E4.9.97.0", {"start": v(11.73, 58.84) * mm, "end": v(10.75, 59.03) * mm});
            skLineSegment(sketch, "E4.1.98.0", {"start": v(6.76, 49.54) * mm, "end": v(8.02, 59.46) * mm});
            skLineSegment(sketch, "E4.3.98.0", {"start": v(6.76, 49.54) * mm, "end": v(5.77, 49.67) * mm});
            skLineSegment(sketch, "E4.6.98.0", {"start": v(5.77, 49.67) * mm, "end": v(7.02, 59.59) * mm});
            skLineSegment(sketch, "E4.9.98.0", {"start": v(8.02, 59.46) * mm, "end": v(7.02, 59.59) * mm});
            skLineSegment(sketch, "E4.1.99.0", {"start": v(3.64, 49.87) * mm, "end": v(4.27, 59.85) * mm});
            skLineSegment(sketch, "E4.3.99.0", {"start": v(3.64, 49.87) * mm, "end": v(2.64, 49.93) * mm});
            skLineSegment(sketch, "E4.6.99.0", {"start": v(2.64, 49.93) * mm, "end": v(3.27, 59.91) * mm});
            skLineSegment(sketch, "E4.9.99.0", {"start": v(4.27, 59.85) * mm, "end": v(3.27, 59.91) * mm});
            skCircle(sketch, "E5", {"center": v(0, 28.5) * mm, "radius": 1 * mm});
            skCircle(sketch, "E6.1.0.0", {"center": v(0, 33.5) * mm, "radius": 1 * mm});
            skCircle(sketch, "E6.2.0.0", {"center": v(0, 38.5) * mm, "radius": 1 * mm});
            skCircle(sketch, "E6.3.0.0", {"center": v(0, 43.5) * mm, "radius": 1 * mm});
            skLineSegment(sketch, "E6.direction1", {"start": v(0, 28.5) * mm, "end": v(0, 33.5) * mm, "construction": true});
            skLineSegment(sketch, "E7.1.0", {"start": v(-24.68, -14.25) * mm, "end": v(-29.01, -16.75) * mm, "construction": true});
            skCircle(sketch, "E7.1.1", {"center": v(-37.67, -21.75) * mm, "radius": 1 * mm});
            skCircle(sketch, "E7.1.2", {"center": v(-33.34, -19.25) * mm, "radius": 1 * mm});
            skCircle(sketch, "E7.1.3", {"center": v(-29.01, -16.75) * mm, "radius": 1 * mm});
            skCircle(sketch, "E7.1.4", {"center": v(-24.68, -14.25) * mm, "radius": 1 * mm});
            skLineSegment(sketch, "E7.2.0", {"start": v(24.68, -14.25) * mm, "end": v(29.01, -16.75) * mm, "construction": true});
            skCircle(sketch, "E7.2.1", {"center": v(37.67, -21.75) * mm, "radius": 1 * mm});
            skCircle(sketch, "E7.2.2", {"center": v(33.34, -19.25) * mm, "radius": 1 * mm});
            skCircle(sketch, "E7.2.3", {"center": v(29.01, -16.75) * mm, "radius": 1 * mm});
            skCircle(sketch, "E7.2.4", {"center": v(24.68, -14.25) * mm, "radius": 1 * mm});
            skSolve(sketch);
        }
        {
            var Q0;
            Q0=makeQuery(id+"F0.imprint","IMPRINT",FACE,{"disambiguationData":[TD([[makeQuery(id+"F0.imprint","IMPRINT",EDGE,{"derivedFrom":sQuery(id+"F0.wireOp",EDGE,"E1")}),-1.0]])]});
            var Q1;
            {var subQ500=sQuery(id+"F0.wireOp",EDGE,"E2.bottom");Q1=makeQuery(id+"F0.imprint","IMPRINT",FACE,{"disambiguationData":[TD([[makeQuery(id+"F0.imprint","IMPRINT",EDGE,{"derivedFrom":subQ500}),1.0]])]});}
            extrude(context, id + "F1", {"entities" : qUnion([Q0, Q1]), "depth" : 10 * mm});
        }
        {
            var Q0;
            Q0=qCreatedBy(makeId("Top.planeOp"),FACE);
            cPlane(context, id + "F2", {"entities" : qUnion([Q0]), "cplaneType" : CPlaneType.OFFSET, "offset" : 25 * mm, "width" : 150 * mm, "height" : 150 * mm});
        }
        {
            var Q0;
            Q0=qCreatedBy(id+"F2.planeOp",FACE);
            var sketch = newSketch(context, id + "F3", { "sketchPlane" : qUnion([Q0])});
            skCircle(sketch, "E8", {"center": v(0, 0) * mm, "radius": 80 * mm});
            skLineSegment(sketch, "E9.bottom", {"start": v(2.35, -0.9) * mm, "end": v(-2.35, -0.9) * mm});
            skLineSegment(sketch, "E9.top", {"start": v(2.35, 0.9) * mm, "end": v(-2.35, 0.9) * mm});
            skLineSegment(sketch, "E9.left", {"start": v(2.35, -0.9) * mm, "end": v(2.35, 0.9) * mm});
            skLineSegment(sketch, "E9.right", {"start": v(-2.35, -0.9) * mm, "end": v(-2.35, 0.9) * mm});
            skLineSegment(sketch, "E10.bottom", {"start": v(0.9, -2.35) * mm, "end": v(-0.9, -2.35) * mm});
            skLineSegment(sketch, "E10.top", {"start": v(0.9, 2.35) * mm, "end": v(-0.9, 2.35) * mm});
            skLineSegment(sketch, "E10.left", {"start": v(0.9, -2.35) * mm, "end": v(0.9, 2.35) * mm});
            skLineSegment(sketch, "E10.right", {"start": v(-0.9, -2.35) * mm, "end": v(-0.9, 2.35) * mm});
            skCircle(sketch, "E11.0", {"center": v(0, 0) * mm, "radius": 25 * mm});
            skCircle(sketch, "E12.0", {"center": v(0, 43.5) * mm, "radius": 1 * mm, "construction": true});
            skCircle(sketch, "E13", {"center": v(0, 43.5) * mm, "radius": 1.5 * mm, "construction": true});
            skCircle(sketch, "E14.0", {"center": v(0, 28.5) * mm, "radius": 1 * mm, "construction": true});
            skCircle(sketch, "E15", {"center": v(0, 28.5) * mm, "radius": 1.5 * mm, "construction": true});
            skLineSegment(sketch, "E16", {"start": v(1.5, 43.5) * mm, "end": v(1.5, 28.5) * mm});
            skLineSegment(sketch, "E17", {"start": v(-1.5, 43.5) * mm, "end": v(-1.5, 28.5) * mm});
            skArc(sketch, "E18", {"start": v(1.5, 43.5) * mm, "mid": v(0, 45) * mm, "end": v(-1.5, 43.5) * mm});
            skArc(sketch, "E19", {"start": v(-1.5, 28.5) * mm, "mid": v(0, 27) * mm, "end": v(1.5, 28.5) * mm});
            skLineSegment(sketch, "E20.1.0", {"start": v(-36.92, -23.05) * mm, "end": v(-23.93, -15.55) * mm});
            skCircle(sketch, "E20.1.1", {"center": v(-37.67, -21.75) * mm, "radius": 1.5 * mm, "construction": true});
            skLineSegment(sketch, "E20.1.2", {"start": v(-38.42, -20.45) * mm, "end": v(-25.43, -12.95) * mm});
            skCircle(sketch, "E20.1.3", {"center": v(-37.67, -21.75) * mm, "radius": 1 * mm, "construction": true});
            skCircle(sketch, "E20.1.4", {"center": v(-24.68, -14.25) * mm, "radius": 1 * mm, "construction": true});
            skCircle(sketch, "E20.1.5", {"center": v(-24.68, -14.25) * mm, "radius": 1.5 * mm, "construction": true});
            skArc(sketch, "E20.1.6", {"start": v(-38.42, -20.45) * mm, "mid": v(-38.97, -22.5) * mm, "end": v(-36.92, -23.05) * mm});
            skArc(sketch, "E20.1.7", {"start": v(-23.93, -15.55) * mm, "mid": v(-23.38, -13.5) * mm, "end": v(-25.43, -12.95) * mm});
            skLineSegment(sketch, "E20.2.0", {"start": v(38.42, -20.45) * mm, "end": v(25.43, -12.95) * mm});
            skCircle(sketch, "E20.2.1", {"center": v(37.67, -21.75) * mm, "radius": 1.5 * mm, "construction": true});
            skLineSegment(sketch, "E20.2.2", {"start": v(36.92, -23.05) * mm, "end": v(23.93, -15.55) * mm});
            skCircle(sketch, "E20.2.3", {"center": v(37.67, -21.75) * mm, "radius": 1 * mm, "construction": true});
            skCircle(sketch, "E20.2.4", {"center": v(24.68, -14.25) * mm, "radius": 1 * mm, "construction": true});
            skCircle(sketch, "E20.2.5", {"center": v(24.68, -14.25) * mm, "radius": 1.5 * mm, "construction": true});
            skArc(sketch, "E20.2.6", {"start": v(36.92, -23.05) * mm, "mid": v(38.97, -22.5) * mm, "end": v(38.42, -20.45) * mm});
            skArc(sketch, "E20.2.7", {"start": v(25.43, -12.95) * mm, "mid": v(23.38, -13.5) * mm, "end": v(23.93, -15.55) * mm});
            skSolve(sketch);
        }
        {
            var Q0;
            Q0=makeQuery(id+"F3.imprint","IMPRINT",FACE,{"disambiguationData":[TD([[makeQuery(id+"F3.imprint","IMPRINT",EDGE,{"derivedFrom":sQuery(id+"F3.wireOp",EDGE,"E8")}),1.0]])]});
            extrude(context, id + "F4", {"entities" : qUnion([Q0]), "depth" : 10 * mm});
        }
    });
